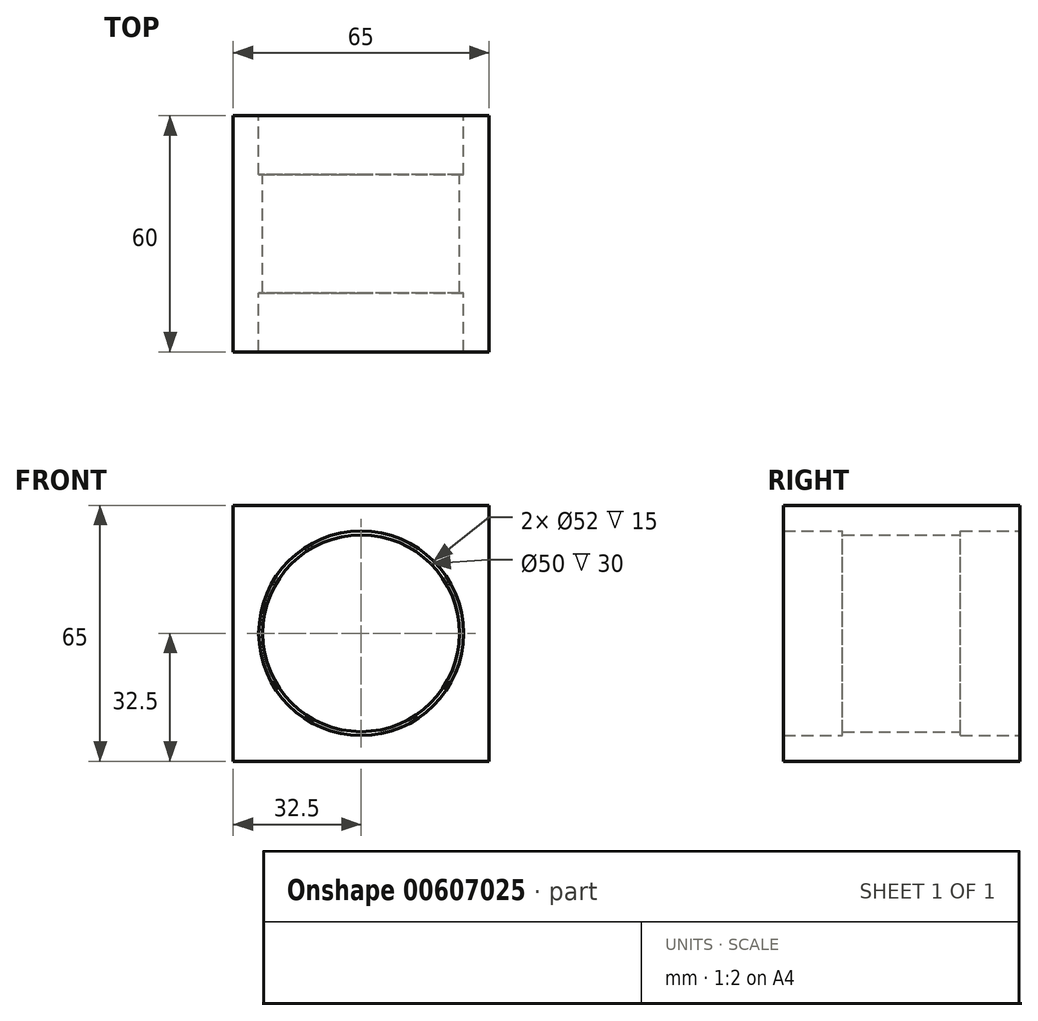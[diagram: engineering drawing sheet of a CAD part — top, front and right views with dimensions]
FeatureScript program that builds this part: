
annotation { "Feature Type Name" : "Feature", "Feature Type Description" : "" }
export const myFeature = defineFeature(function(context is Context, id is Id, definition is map)
    precondition{}
    {
        {
            var Q0;
            Q0=qCreatedBy(makeId("Front.planeOp"),FACE);
            var sketch = newSketch(context, id + "F0", { "sketchPlane" : qUnion([Q0]) });
            skCircle(sketch, "E0", {"center": v(0, 0) * mm, "radius": 26 * mm});
            skLineSegment(sketch, "E1.bottom", {"start": v(32.5, 32.5) * mm, "end": v(-32.5, 32.5) * mm});
            skLineSegment(sketch, "E1.top", {"start": v(32.5, -32.5) * mm, "end": v(-32.5, -32.5) * mm});
            skLineSegment(sketch, "E1.left", {"start": v(32.5, 32.5) * mm, "end": v(32.5, -32.5) * mm});
            skLineSegment(sketch, "E1.right", {"start": v(-32.5, 32.5) * mm, "end": v(-32.5, -32.5) * mm});
            skSolve(sketch);
        }
        {
            var Q0;
            Q0=makeQuery(id+"F0.imprint","IMPRINT",FACE,{"disambiguationData":[TD([[makeQuery(id+"F0.imprint","IMPRINT",EDGE,{"derivedFrom":sQuery(id+"F0.wireOp",EDGE,"E0")}),-1.0]])]});
            extrude(context, id + "F1", {"entities" : qUnion([Q0]), "depth" : 60 * mm, "offsetDistance" : 25 * mm});
        }
        {
            var Q0;
            Q0=qCreatedBy(makeId("Front.planeOp"),FACE);
            cPlane(context, id + "F2", {"entities" : qUnion([Q0]), "cplaneType" : CPlaneType.OFFSET, "offset" : 30 * mm, "width" : 150 * mm, "height" : 150 * mm});
        }
        {
            var Q0;
            Q0=qCreatedBy(id+"F2.planeOp",FACE);
            var sketch = newSketch(context, id + "F3", { "sketchPlane" : qUnion([Q0]) });
            skCircle(sketch, "E2", {"center": v(0, 0) * mm, "radius": 26 * mm});
            skCircle(sketch, "E3", {"center": v(0, 0) * mm, "radius": 25 * mm});
            skSolve(sketch);
        }
        {
            var Q0;
            Q0=makeQuery(id+"F3.imprint","IMPRINT",FACE,{"disambiguationData":[TD([[makeQuery(id+"F3.imprint","IMPRINT",EDGE,{"derivedFrom":sQuery(id+"F3.wireOp",EDGE,"E2")}),1.0]])]});
            extrude(context, id + "F4", {"entities" : qUnion([Q0]), "operationType" : NewBodyOperationType.ADD, "endBound" : BoundingType.SYMMETRIC, "depth" : 30 * mm, "offsetDistance" : 25 * mm});
        }
    });
